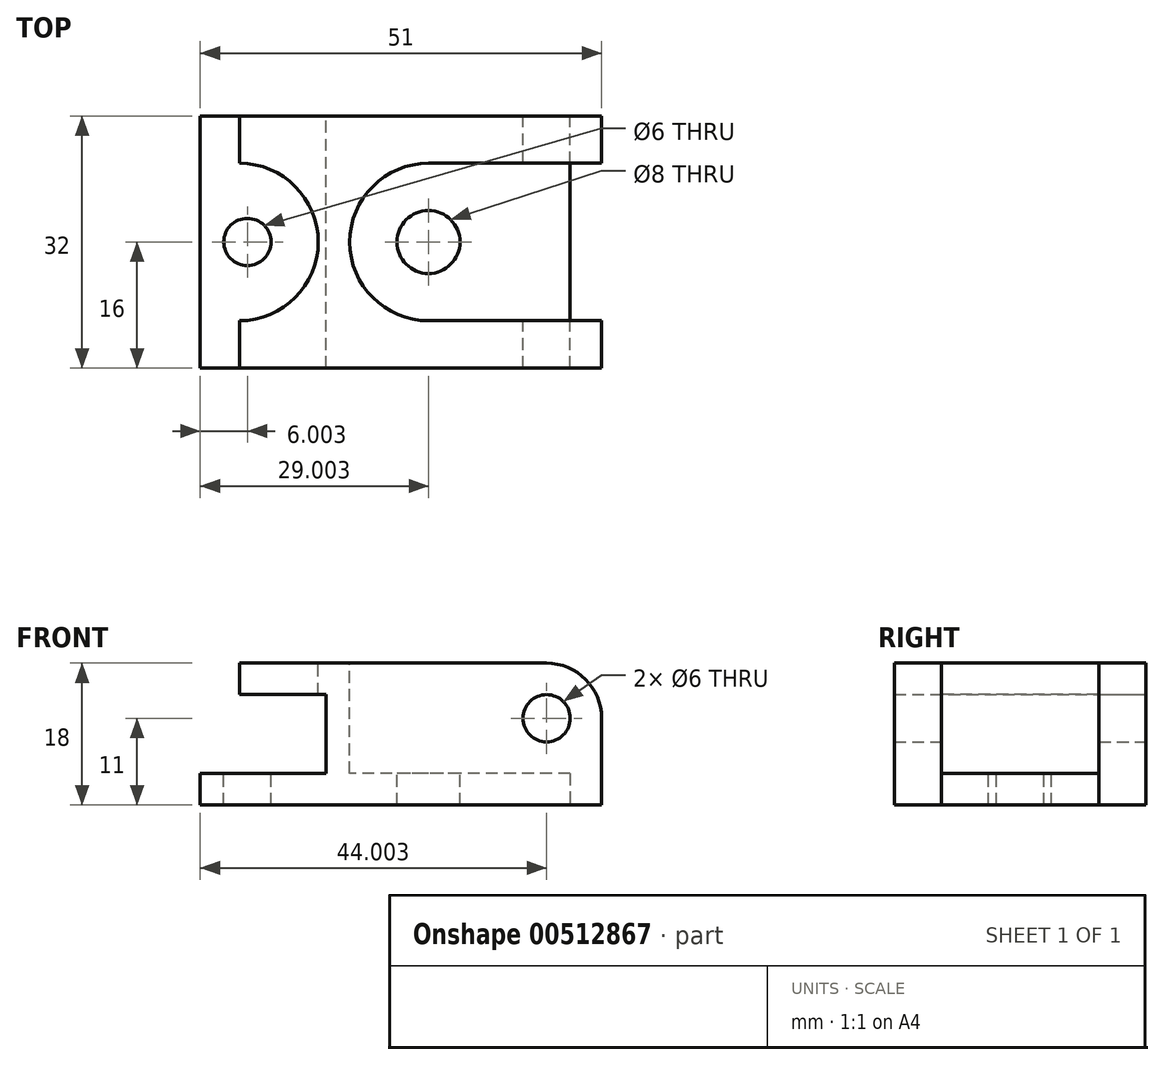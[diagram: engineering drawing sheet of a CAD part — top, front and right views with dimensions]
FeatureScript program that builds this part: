
annotation { "Feature Type Name" : "Feature", "Feature Type Description" : "" }
export const myFeature = defineFeature(function(context is Context, id is Id, definition is map)
    precondition{}
    {
        {
            var Q0;
            Q0=qCreatedBy(makeId("Front.planeOp"),FACE);
            var sketch = newSketch(context, id + "F0", { "sketchPlane" : qUnion([Q0])});
            skLineSegment(sketch, "E0", {"start": v(-11.5, 0) * mm, "end": v(-11.5, 4) * mm});
            skLineSegment(sketch, "E1", {"start": v(-11.5, 4) * mm, "end": v(4.5, 4) * mm});
            skLineSegment(sketch, "E2", {"start": v(4.5, 4) * mm, "end": v(4.5, 14) * mm});
            skLineSegment(sketch, "E3", {"start": v(4.5, 14) * mm, "end": v(-6.5, 14) * mm});
            skLineSegment(sketch, "E4", {"start": v(-6.5, 14) * mm, "end": v(-6.5, 18) * mm});
            skLineSegment(sketch, "E5", {"start": v(-6.5, 18) * mm, "end": v(32.5, 18) * mm});
            skLineSegment(sketch, "E6", {"start": v(39.5, 11) * mm, "end": v(39.5, 0) * mm});
            skLineSegment(sketch, "E7", {"start": v(39.5, 0) * mm, "end": v(-11.5, 0) * mm});
            skPoint(sketch, "E8.visualSharp", {"position": v(39.5, 18) * mm});
            skArc(sketch, "E8.filletArc", {"start": v(39.5, 11) * mm, "mid": v(37.44, 15.95) * mm, "end": v(32.5, 18) * mm});
            skCircle(sketch, "E9", {"center": v(32.5, 11) * mm, "radius": 3 * mm});
            skSolve(sketch);
        }
        {
            var Q0;
            Q0 = qSketchRegion(id + "F0", true);
            extrude(context, id + "F1", {"entities" : qUnion([Q0]), "endBound" : BoundingType.SYMMETRIC, "depth" : 32 * mm, "offsetDistance" : 25 * mm});
        }
        {
            var Q0;
            Q0=makeQuery(id+"F1.opExtrude","SWEPT_FACE",FACE,{"disambiguationData":[OSD([sQuery(id+"F0.wireOp",EDGE,"E5")])]});
            var sketch = newSketch(context, id + "F2", { "sketchPlane" : qUnion([Q0])});
            skLineSegment(sketch, "E10", {"start": v(-6.5, 16) * mm, "end": v(-6.5, 10) * mm});
            skLineSegment(sketch, "E11", {"start": v(-6.5, -16) * mm, "end": v(-6.5, -10) * mm});
            skArc(sketch, "E12", {"start": v(-6.5, -10) * mm, "mid": v(3.5, 0) * mm, "end": v(-6.5, 10) * mm});
            skLineSegment(sketch, "E13", {"start": v(32.5, 16) * mm, "end": v(32.5, 10) * mm});
            skLineSegment(sketch, "E14", {"start": v(32.5, -16) * mm, "end": v(32.5, -10) * mm});
            skLineSegment(sketch, "E15", {"start": v(32.5, 10) * mm, "end": v(17.5, 10) * mm});
            skLineSegment(sketch, "E16", {"start": v(32.5, -10) * mm, "end": v(17.5, -10) * mm});
            skArc(sketch, "E17", {"start": v(17.5, 10) * mm, "mid": v(7.5, 0) * mm, "end": v(17.5, -10) * mm});
            skLineSegment(sketch, "E18", {"start": v(32.5, 10) * mm, "end": v(44.1, 10) * mm});
            skLineSegment(sketch, "E19", {"start": v(44.1, 10) * mm, "end": v(44.1, -10) * mm});
            skLineSegment(sketch, "E20", {"start": v(44.1, -10) * mm, "end": v(32.5, -10) * mm});
            skSolve(sketch);
        }
        {
            var Q0;
            Q0 = qSketchRegion(id + "F2", true);
            var Q1;
            {var subQ0=sQuery(id+"F2.wireOp",EDGE,"E12");Q1=makeQuery(id+"F2.imprint","IMPRINT",FACE,{"disambiguationData":[TD([[makeQuery(id+"F2.imprint","IMPRINT",EDGE,{"derivedFrom":subQ0}),1.0]])]});}
            extrude(context, id + "F3", {"entities" : qUnion([Q0, Q1]), "operationType" : NewBodyOperationType.REMOVE, "oppositeDirection" : true, "depth" : 14 * mm, "offsetDistance" : 25 * mm});
        }
        {
            var Q0;
            Q0=makeQuery(id+"F1.opExtrude","SWEPT_FACE",FACE,{"disambiguationData":[OSD([sQuery(id+"F0.wireOp",EDGE,"E6")])]});
            var sketch = newSketch(context, id + "F4", { "sketchPlane" : qUnion([Q0])});
            skLineSegment(sketch, "E21", {"start": v(-10, 4) * mm, "end": v(-10, 0) * mm});
            skLineSegment(sketch, "E22", {"start": v(10, 4) * mm, "end": v(10, 0) * mm});
            skSolve(sketch);
        }
        {
            var Q0;
            Q0 = qSketchRegion(id + "F4", true);
            var Q1;
            {var subQ0=sQuery(id+"F4.wireOp",EDGE,"E21");Q1=makeQuery(id+"F4.imprint","IMPRINT",FACE,{"disambiguationData":[TD([[makeQuery(id+"F4.imprint","IMPRINT",EDGE,{"derivedFrom":subQ0}),1.0]])]});}
            extrude(context, id + "F5", {"entities" : qUnion([Q0, Q1]), "operationType" : NewBodyOperationType.REMOVE, "oppositeDirection" : true, "depth" : 4 * mm, "offsetDistance" : 25 * mm});
        }
        {
            var Q0;
            Q0=makeQuery(id+"F1.opExtrude","SWEPT_FACE",FACE,{"disambiguationData":[OSD([sQuery(id+"F0.wireOp",EDGE,"E1")])]});
            var sketch = newSketch(context, id + "F6", { "sketchPlane" : qUnion([Q0])});
            skCircle(sketch, "E23", {"center": v(-5.5, 0) * mm, "radius": 3 * mm});
            skSolve(sketch);
        }
        {
            var Q0;
            Q0 = qSketchRegion(id + "F6", true);
            extrude(context, id + "F7", {"entities" : qUnion([Q0]), "operationType" : NewBodyOperationType.REMOVE, "oppositeDirection" : true, "depth" : 25 * mm, "offsetDistance" : 25 * mm});
        }
        {
            var Q0;
            Q0=makeQuery(id+"F3.boolean.opBoolean","COPY",FACE,{"derivedFrom":makeQuery(id+"F3.opExtrude","CAP_FACE",FACE,{"disambiguationData":[OSD([sQuery(id+"F2.wireOp",EDGE,"E15"),sQuery(id+"F2.wireOp",EDGE,"E16"),sQuery(id+"F2.wireOp",EDGE,"E17"),sQuery(id+"F2.wireOp",EDGE,"E18"),sQuery(id+"F2.wireOp",EDGE,"E19"),sQuery(id+"F2.wireOp",EDGE,"E20")])],"isStart":false})});
            var sketch = newSketch(context, id + "F8", { "sketchPlane" : qUnion([Q0])});
            skCircle(sketch, "E24", {"center": v(17.5, 0) * mm, "radius": 4 * mm});
            skSolve(sketch);
        }
        {
            var Q0;
            Q0=makeQuery(id+"F8.imprint","IMPRINT",FACE,{"disambiguationData":[TD([[makeQuery(id+"F8.imprint","IMPRINT",EDGE,{"derivedFrom":sQuery(id+"F8.wireOp",EDGE,"E24")}),1.0]])]});
            extrude(context, id + "F9", {"entities" : qUnion([Q0]), "operationType" : NewBodyOperationType.REMOVE, "oppositeDirection" : true, "depth" : 25 * mm, "offsetDistance" : 25 * mm});
        }
    });
